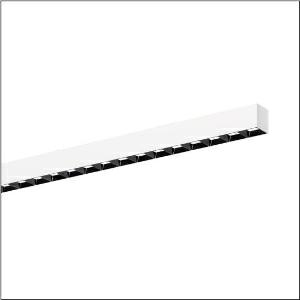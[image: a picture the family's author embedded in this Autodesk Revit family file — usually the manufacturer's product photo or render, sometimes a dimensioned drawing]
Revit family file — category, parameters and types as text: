
# Revit family: silica_r__21_51mx21dc3awb_ae09
name_source: partatom
category: Lighting Fixtures
units: mm (PartAtom-declared; Revit-internal decimal feet)

## family parameters
Cut with Voids When Loaded = No
Host = Face
Light Source = No
Part Type = Normal
Room Calculation Point = No
Round Connector Dimension = Use Diameter
Shared = No

## types (1)
- --- (1 x LED, 10800 lm, 69.3 W, 3000K)
    Apparent Load = 69 VA
    CIE Flux Codes = 87 99 100 100 100
    Color Rendering = 80
    Color Temperature = 3000K
    Default Elevation = 1800 mm
    Description = Silica® 21, office luminaire, primary light control with darklight reflector, of PMMA, black, CAT 2 (L<= 3000cd/m²), light emission: direct distribution, primary light characteristic: symmetric, installation type: surface-mounted, LED, rated luminous flux: 10.800lm, luminous efficacy: 156lm/W, light colour: 830, colour temperature: 3000K, with terminal, 3+2-pole, max. 2.5mm², mains connection: 220..240V, AC, 50/60Hz, luminaire housing, of aluminium, traffic white (RAL 9016), length: 3.004mm, width: 53mm, height: 53mm, protection rating (complete): IP20, insulation class (complete): insulation class I (protective earthing), certification: CE, permissible operating ambient temperature: 0..+35°C, standard: EN 50419, packaging unit: 1 piece
    Height = 0 mm  [stored 0 ft]
    Lamp = 1 x LED
    Lamp Light Flux = 10800 lm
    Lamp Power = 69.3 W
    Lamp count = 1
    Length = 3004 mm
    Luminous efficacy = 156 lm/W
    Manufacturer = Siteco
    ModVariant = No
    Model = 51MX21DC3AWB
    Mounting Place = Ceiling
    Mounting Type = Recessed
    Number of Poles = 1
    OnlyDefault = Yes
    Power Factor = 1
    Product Name = Silica® 21
    Product group = office luminaire | ceiling recessed
    ProductGroupID = 401
    Protection Class = Protection class I
    Protection Degree = IP 20
    RLX_Detail_Level = 1
    RLX_Emergency_Light_Flux = 0 lm
    RLX_Emergency_Type = 0
    RLX_Emergency_Type_DB = No
    RlxData = <blob elided: 62165 chars, md5=e19ca1bf>
    Socket = socket
    Standby Power = 0 W
    System Light Flux = 10800 lm
    System Power = 69 W
    Type Comments = factory setting: luminous flux: 100 % | dim-lin: 254 | 393 mA
    Type Image = l_1313592.jpg
    URL = http://relux.com
    VarID = @adj_072937
    Voltage = 0 V
    Weight = 0.00 kg
    Width = 53 mm

note: [stored X ft] marks values corroborated as IEEE doubles in the binary element streams (Revit-internal decimal feet)

## geometry (parser evidence)
native form markers: Blend x4, Sweep x10
no freeform markers — native parametric forms only
